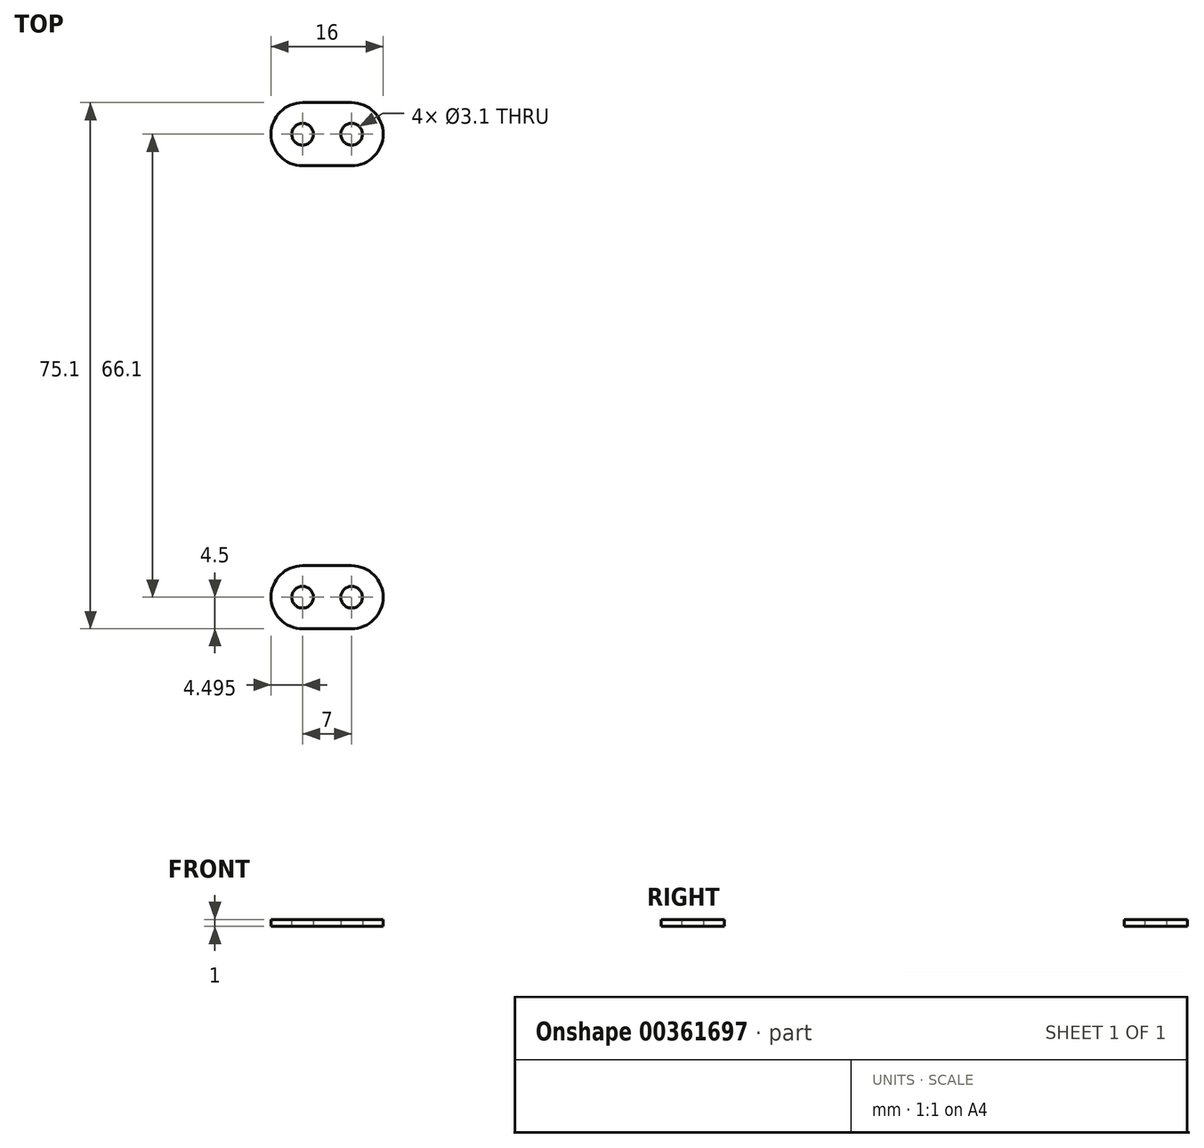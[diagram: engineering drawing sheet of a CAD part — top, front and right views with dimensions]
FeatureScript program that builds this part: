
annotation { "Feature Type Name" : "Feature", "Feature Type Description" : "" }
export const myFeature = defineFeature(function(context is Context, id is Id, definition is map)
    precondition{}
    {
        {
            var Q0;
            Q0=qCreatedBy(makeId("Top.planeOp"),FACE);
            var sketch = newSketch(context, id + "F0", { "sketchPlane" : qUnion([Q0])});
            skLineSegment(sketch, "E0.left", {"start": v(24.35, 33.05) * mm, "end": v(24.35, 33.05) * mm});
            skArc(sketch, "E1.filletArc", {"start": v(24.35, 33.05) * mm, "mid": v(23.03, 36.23) * mm, "end": v(19.85, 37.55) * mm});
            skCircle(sketch, "E2", {"center": v(19.85, 33.05) * mm, "radius": 1.55 * mm});
            skCircle(sketch, "E3", {"center": v(12.85, 33.05) * mm, "radius": 1.55 * mm});
            skArc(sketch, "E4.filletArc", {"start": v(19.85, 28.55) * mm, "mid": v(23.03, 29.87) * mm, "end": v(24.35, 33.05) * mm});
            skLineSegment(sketch, "E5", {"start": v(8.35, 33.05) * mm, "end": v(8.35, 33.05) * mm});
            skLineSegment(sketch, "E6", {"start": v(19.85, 37.55) * mm, "end": v(12.85, 37.55) * mm});
            skLineSegment(sketch, "E7", {"start": v(19.85, 28.55) * mm, "end": v(12.85, 28.55) * mm});
            skArc(sketch, "E8.filletArc", {"start": v(8.35, 33.05) * mm, "mid": v(9.66, 29.87) * mm, "end": v(12.85, 28.55) * mm});
            skArc(sketch, "E9.filletArc", {"start": v(12.85, 37.55) * mm, "mid": v(9.66, 36.23) * mm, "end": v(8.35, 33.05) * mm});
            skLineSegment(sketch, "E10.MirrorCS", {"start": v(19.85, -37.55) * mm, "end": v(12.85, -37.55) * mm});
            skArc(sketch, "E11.MirrorCS", {"start": v(24.35, -33.05) * mm, "mid": v(23.03, -36.23) * mm, "end": v(19.85, -37.55) * mm});
            skArc(sketch, "E12.MirrorCS", {"start": v(19.85, -28.55) * mm, "mid": v(23.03, -29.87) * mm, "end": v(24.35, -33.05) * mm});
            skLineSegment(sketch, "E13.MirrorCS", {"start": v(19.85, -28.55) * mm, "end": v(12.85, -28.55) * mm});
            skArc(sketch, "E14.MirrorCS", {"start": v(8.35, -33.05) * mm, "mid": v(9.66, -29.87) * mm, "end": v(12.85, -28.55) * mm});
            skArc(sketch, "E15.MirrorCS", {"start": v(12.85, -37.55) * mm, "mid": v(9.66, -36.23) * mm, "end": v(8.35, -33.05) * mm});
            skCircle(sketch, "E16.MirrorC", {"center": v(12.85, -33.05) * mm, "radius": 1.55 * mm});
            skCircle(sketch, "E17.MirrorC", {"center": v(19.85, -33.05) * mm, "radius": 1.55 * mm});
            skSolve(sketch);
        }
        {
            var Q0;
            Q0=qSketchRegion(id+"F0",true);
            extrude(context, id + "F1", {"entities" : qUnion([Q0]), "depth" : 1 * mm});
        }
    });
